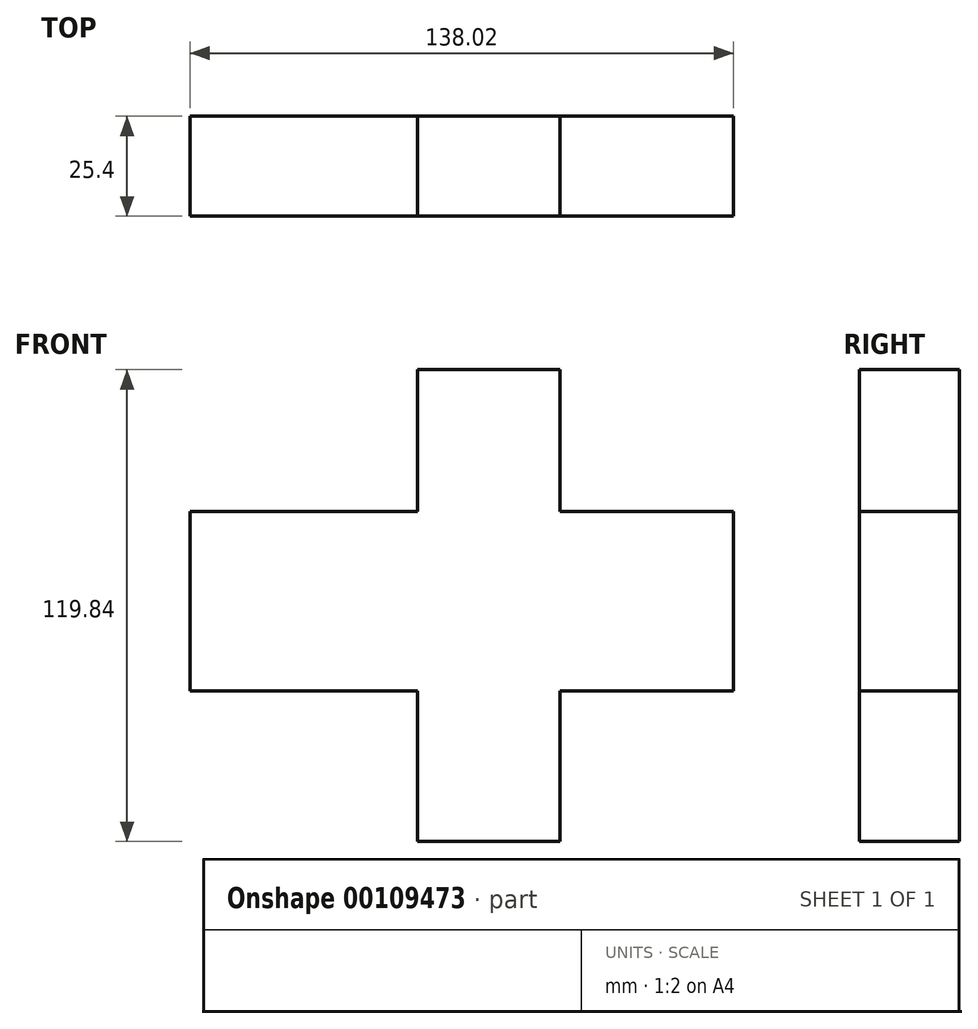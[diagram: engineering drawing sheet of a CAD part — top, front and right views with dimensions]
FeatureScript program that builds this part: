
annotation { "Feature Type Name" : "Feature", "Feature Type Description" : "" }
export const myFeature = defineFeature(function(context is Context, id is Id, definition is map)
    precondition{}
    {
        {
            var Q0;
            Q0=qCreatedBy(makeId("Front.planeOp"),FACE);
            var sketch = newSketch(context, id + "F0", { "sketchPlane" : qUnion([Q0])});
            skLineSegment(sketch, "E0.bottom", {"start": v(61.28, 19.97) * mm, "end": v(-76.74, 19.97) * mm});
            skLineSegment(sketch, "E0.top", {"start": v(61.28, -25.52) * mm, "end": v(-76.74, -25.52) * mm});
            skLineSegment(sketch, "E0.left", {"start": v(61.28, 19.97) * mm, "end": v(61.28, -25.52) * mm});
            skLineSegment(sketch, "E0.right", {"start": v(-76.74, 19.97) * mm, "end": v(-76.74, -25.52) * mm});
            skSolve(sketch);
        }
        {
            var Q0;
            Q0 = qSketchRegion(id + "F0", true);
            extrude(context, id + "F1", {"entities" : qUnion([Q0]), "depth" : 25.4 * mm});
        }
        {
            var Q0;
            Q0=qCreatedBy(makeId("Front.planeOp"),FACE);
            var sketch = newSketch(context, id + "F2", { "sketchPlane" : qUnion([Q0])});
            skLineSegment(sketch, "E1.bottom", {"start": v(17.25, 56.05) * mm, "end": v(-18.97, 56.05) * mm});
            skLineSegment(sketch, "E1.top", {"start": v(17.25, -63.79) * mm, "end": v(-18.97, -63.79) * mm});
            skLineSegment(sketch, "E1.left", {"start": v(17.25, 56.05) * mm, "end": v(17.25, -63.79) * mm});
            skLineSegment(sketch, "E1.right", {"start": v(-18.97, 56.05) * mm, "end": v(-18.97, -63.79) * mm});
            skSolve(sketch);
        }
        {
            var Q0;
            Q0 = qSketchRegion(id + "F2", true);
            extrude(context, id + "F3", {"entities" : qUnion([Q0]), "operationType" : NewBodyOperationType.ADD, "depth" : 25.4 * mm});
        }
    });
